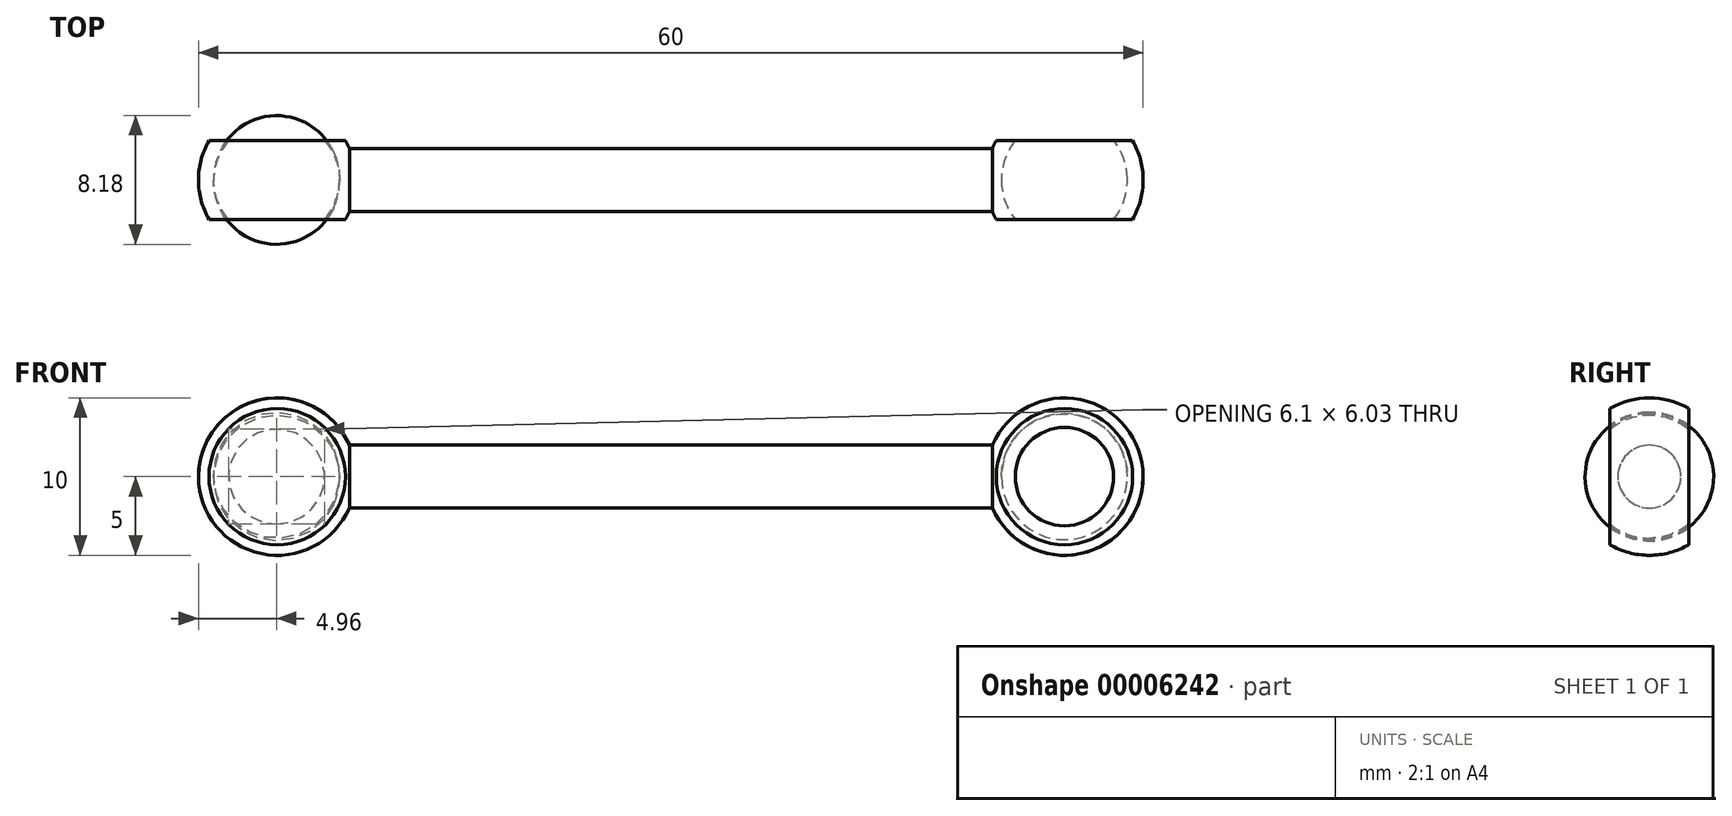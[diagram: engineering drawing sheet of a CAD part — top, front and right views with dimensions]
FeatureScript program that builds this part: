
annotation { "Feature Type Name" : "Feature", "Feature Type Description" : "" }
export const myFeature = defineFeature(function(context is Context, id is Id, definition is map)
    precondition{}
    {
        {
            var Q0;
            Q0=qCreatedBy(makeId("Front.planeOp"),FACE);
            var sketch = newSketch(context, id + "F0", { "sketchPlane" : qUnion([Q0])});
            skArc(sketch, "E0", {"start": v(4.58, 2) * mm, "mid": v(-1.02, 4.9) * mm, "end": v(-5, 0) * mm});
            skArc(sketch, "E1", {"start": v(55, 0) * mm, "mid": v(51.02, 4.9) * mm, "end": v(45.42, 2) * mm});
            skLineSegment(sketch, "E2", {"start": v(4.58, 2) * mm, "end": v(45.42, 2) * mm});
            skPoint(sketch, "E3.start.orphan", {"position": v(5, 0) * mm});
            skLineSegment(sketch, "E4", {"start": v(-5, 0) * mm, "end": v(55, 0) * mm});
            skSolve(sketch);
        }
        {
            var Q0;
            Q0=makeQuery(id+"F0.imprint","IMPRINT",FACE,{"disambiguationData":[TD([[makeQuery(id+"F0.imprint","IMPRINT",EDGE,{"derivedFrom":sQuery(id+"F0.wireOp",EDGE,"E0")}),1.0]])]});
            var Q1;
            Q1=sQuery(id+"F0.wireOp",EDGE,"E4");
            revolve(context, id + "F1", {"entities" : qUnion([Q0]), "axis" : qUnion([Q1]), "revolveType" : RevolveType.FULL});
        }
        {
            var Q0;
            Q0=qCreatedBy(makeId("Right.planeOp"),FACE);
            var sketch = newSketch(context, id + "F2", { "sketchPlane" : qUnion([Q0])});
            skLineSegment(sketch, "E5.rect.bottom", {"start": v(2.5, 7.67) * mm, "end": v(-2.5, 7.67) * mm});
            skLineSegment(sketch, "E5.rect.top", {"start": v(2.5, -7.67) * mm, "end": v(-2.5, -7.67) * mm});
            skLineSegment(sketch, "E5.rect.left", {"start": v(2.5, 7.67) * mm, "end": v(2.5, -7.67) * mm});
            skLineSegment(sketch, "E5.rect.right", {"start": v(-2.5, 7.67) * mm, "end": v(-2.5, -7.67) * mm});
            skPoint(sketch, "E5.rect.middle", {"position": v(0, 0) * mm});
            skLineSegment(sketch, "E6.rect.bottom", {"start": v(7.35, 11.17) * mm, "end": v(-7.35, 11.17) * mm});
            skLineSegment(sketch, "E6.rect.top", {"start": v(7.35, -11.17) * mm, "end": v(-7.35, -11.17) * mm});
            skLineSegment(sketch, "E6.rect.left", {"start": v(7.35, 11.17) * mm, "end": v(7.35, -11.17) * mm});
            skLineSegment(sketch, "E6.rect.right", {"start": v(-7.35, 11.17) * mm, "end": v(-7.35, -11.17) * mm});
            skLineSegment(sketch, "E7.rect.bottom", {"start": v(-1.14, 11.17) * mm, "end": v(1.14, 11.17) * mm});
            skPoint(sketch, "E7.rect.middle", {"position": v(0, 7.67) * mm});
            skPoint(sketch, "E7.rect.top.end.orphan", {"position": v(1.14, 4.17) * mm});
            skPoint(sketch, "E7.rect.top.start.orphan", {"position": v(-1.14, 4.17) * mm});
            skSolve(sketch);
        }
        {
            var Q0;
            Q0=makeQuery(id+"F2.imprint","IMPRINT",FACE,{"disambiguationData":[TD([[makeQuery(id+"F2.imprint","IMPRINT",EDGE,{"derivedFrom":sQuery(id+"F2.wireOp",EDGE,"E5.rect.bottom")}),-1.0]])]});
            extrude(context, id + "F3", {"entities" : qUnion([Q0]), "operationType" : NewBodyOperationType.REMOVE, "oppositeDirection" : true, "depth" : 200 * mm, "symmetric" : true});
        }
        {
            var Q0;
            Q0=qCreatedBy(makeId("Front.planeOp"),FACE);
            var sketch = newSketch(context, id + "F4", { "sketchPlane" : qUnion([Q0])});
            skArc(sketch, "E8", {"start": v(3.96, 0) * mm, "mid": v(-0.04, 3.91) * mm, "end": v(-4.04, 0) * mm});
            skLineSegment(sketch, "E9", {"start": v(-4.04, 0) * mm, "end": v(3.96, 0) * mm});
            skSolve(sketch);
        }
        {
            var Q0;
            Q0=makeQuery(id+"F4.imprint","IMPRINT",FACE,{"disambiguationData":[TD([[makeQuery(id+"F4.imprint","IMPRINT",EDGE,{"derivedFrom":sQuery(id+"F4.wireOp",EDGE,"E8")}),1.0]])]});
            var Q1;
            Q1=sQuery(id+"F4.wireOp",EDGE,"E9");
            revolve(context, id + "F5", {"operationType" : NewBodyOperationType.REMOVE, "entities" : qUnion([Q0]), "axis" : qUnion([Q1]), "revolveType" : RevolveType.FULL, "oppositeDirection" : true});
        }
        {
            var Q0;
            Q0=qCreatedBy(makeId("Front.planeOp"),FACE);
            var sketch = newSketch(context, id + "F6", { "sketchPlane" : qUnion([Q0])});
            skArc(sketch, "E10", {"start": v(54, 0) * mm, "mid": v(50, 4) * mm, "end": v(46, 0) * mm});
            skLineSegment(sketch, "E11", {"start": v(46, 0) * mm, "end": v(54, 0) * mm});
            skSolve(sketch);
        }
        {
            var Q0;
            Q0=makeQuery(id+"F6.imprint","IMPRINT",FACE,{"disambiguationData":[TD([[makeQuery(id+"F6.imprint","IMPRINT",EDGE,{"derivedFrom":sQuery(id+"F6.wireOp",EDGE,"E10")}),1.0]])]});
            var Q1;
            Q1=sQuery(id+"F6.wireOp",EDGE,"E11");
            revolve(context, id + "F7", {"operationType" : NewBodyOperationType.REMOVE, "entities" : qUnion([Q0]), "axis" : qUnion([Q1]), "revolveType" : RevolveType.FULL, "oppositeDirection" : true});
        }
    });
